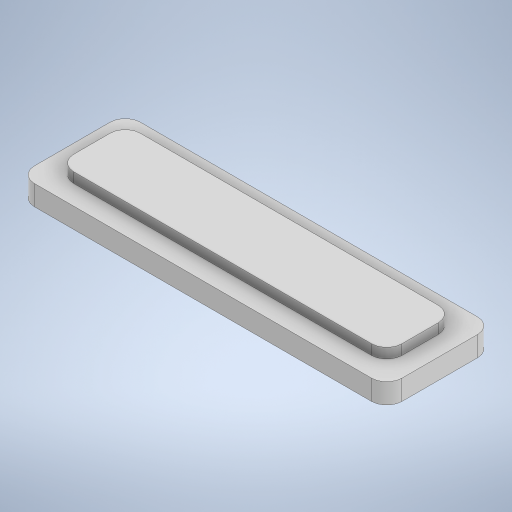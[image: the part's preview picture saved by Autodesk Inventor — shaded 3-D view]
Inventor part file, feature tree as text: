
AUTODESK INVENTOR PART (.ipt)
format: ipt  version: 2024 (Build 280153000, 153)  size: 259,584 bytes
history: native  units: mm
features: extrude x2, sketch x1
ambient origin geometry x8: Origin, YZ Plane, XZ Plane, XY Plane, X Axis, Y Axis, Z Axis, Center Point
bodies: Body1 (feature_tree)
feature tree (3):
  sketch  "Эскиз1"
  extrude  "Выдавливание3"  Depth=1.5mm
  extrude  "Выдавливание4"  Depth=1.5mm
